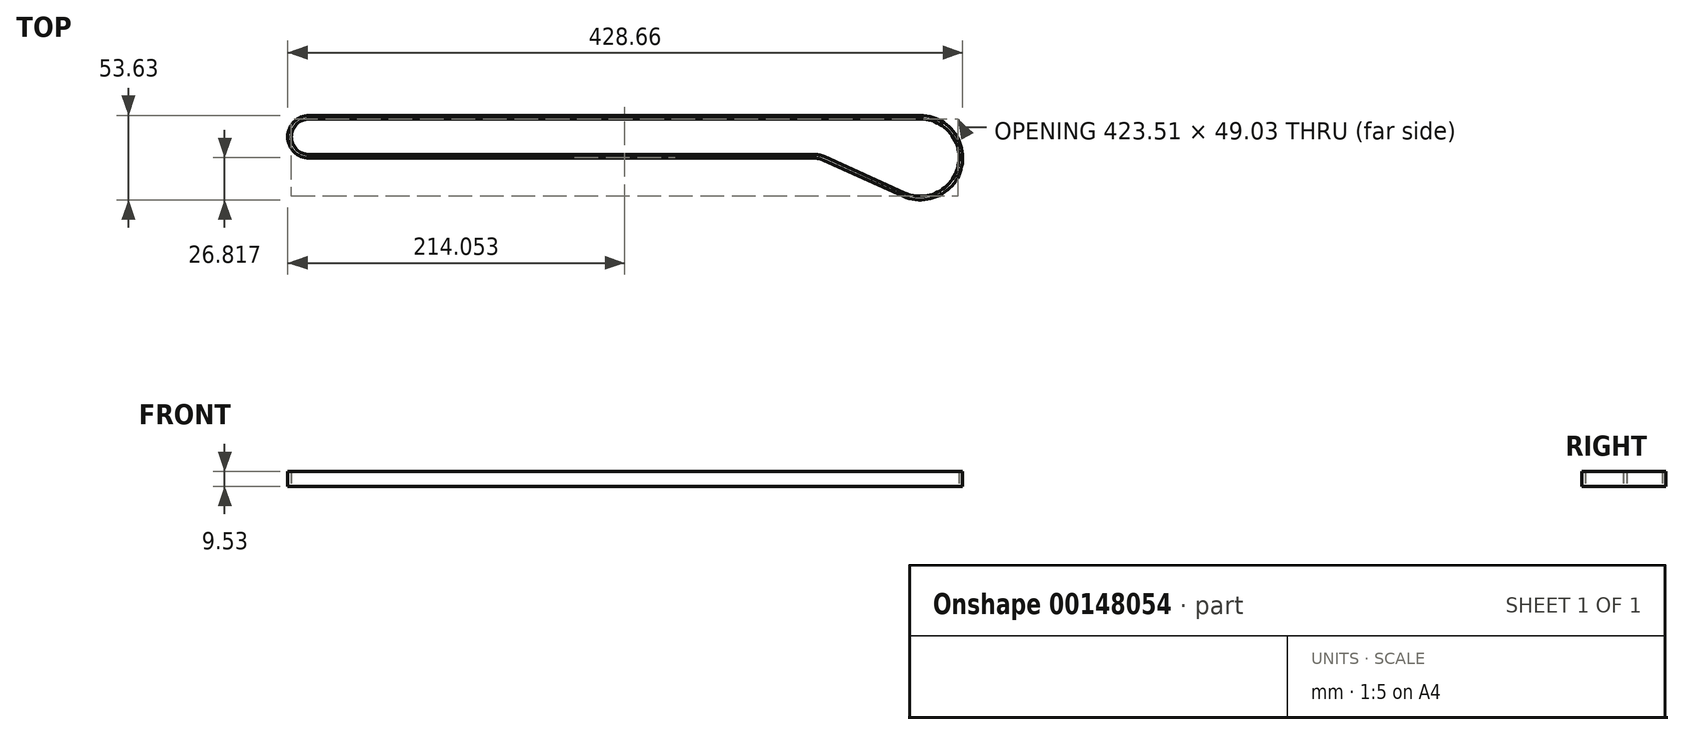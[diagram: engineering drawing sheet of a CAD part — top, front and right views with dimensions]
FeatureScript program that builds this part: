
annotation { "Feature Type Name" : "Feature", "Feature Type Description" : "" }
export const myFeature = defineFeature(function(context is Context, id is Id, definition is map)
    precondition{}
    {
        {
            var Q0;
            Q0=qCreatedBy(makeId("Top.planeOp"),FACE);
            var sketch = newSketch(context, id + "F0", { "sketchPlane" : qUnion([Q0])});
            skArc(sketch, "E0", {"start": v(-10.1, -46.86) * mm, "mid": v(23.97, -29.68) * mm, "end": v(0, 0) * mm});
            skLineSegment(sketch, "E1", {"start": v(0, 0) * mm, "end": v(-388.26, 0) * mm});
            skLineSegment(sketch, "E2", {"start": v(0, 0) * mm, "end": v(0, 2.3) * mm, "construction": true});
            skLineSegment(sketch, "E3", {"start": v(-388.26, 0) * mm, "end": v(-388.26, 2.3) * mm, "construction": true});
            skLineSegment(sketch, "E4", {"start": v(-388.26, 2.3) * mm, "end": v(0, 2.3) * mm});
            skLineSegment(sketch, "E5", {"start": v(-194.13, 0) * mm, "end": v(-194.13, -37.56) * mm, "construction": true});
            skLineSegment(sketch, "E6", {"start": v(-194.13, -37.56) * mm, "end": v(-67.13, -37.56) * mm, "construction": true});
            skArc(sketch, "E7", {"start": v(-61.9, -25.98) * mm, "mid": v(-64.46, -25.14) * mm, "end": v(-67.13, -24.86) * mm});
            skLineSegment(sketch, "E8", {"start": v(-67.13, -24.86) * mm, "end": v(-388.26, -24.86) * mm});
            skLineSegment(sketch, "E9", {"start": v(-67.13, -24.86) * mm, "end": v(-67.13, -22.56) * mm, "construction": true});
            skLineSegment(sketch, "E10", {"start": v(-388.26, -22.56) * mm, "end": v(-67.13, -22.56) * mm});
            skArc(sketch, "E11", {"start": v(-60.96, -23.88) * mm, "mid": v(-63.97, -22.9) * mm, "end": v(-67.13, -22.56) * mm});
            skArc(sketch, "E12", {"start": v(-11.04, -48.96) * mm, "mid": v(26.22, -30.16) * mm, "end": v(0, 2.3) * mm});
            skLineSegment(sketch, "E13", {"start": v(-60.96, -23.88) * mm, "end": v(-10.1, -46.86) * mm});
            skLineSegment(sketch, "E14", {"start": v(-61.9, -25.98) * mm, "end": v(-11.04, -48.96) * mm});
            skArc(sketch, "E15", {"start": v(-388.26, 2.3) * mm, "mid": v(-401.84, -11.28) * mm, "end": v(-388.26, -24.86) * mm});
            skArc(sketch, "E16", {"start": v(-388.26, 0) * mm, "mid": v(-399.54, -11.28) * mm, "end": v(-388.26, -22.56) * mm});
            skSolve(sketch);
        }
        {
            var Q0;
            Q0=qSketchRegion(id+"F0",true);
            extrude(context, id + "F1", {"entities" : qUnion([Q0]), "depth" : 9.52 * mm});
        }
    });
